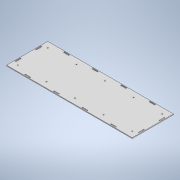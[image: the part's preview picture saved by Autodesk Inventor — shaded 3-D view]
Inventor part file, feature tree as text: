
AUTODESK INVENTOR PART (.ipt)
format: ipt  version: 2022 (Build 260153000, 153)  size: 268,288 bytes
history: native  units: in
note: dims shown in document units (in); Inventor stores cm internally (conversion verified against a paired STEP export)
features: extrude x1, sketch x1
ambient origin geometry x8: Origin, YZ Plane, XZ Plane, XY Plane, X Axis, Y Axis, Z Axis, Center Point
bodies: Body1 (feature_tree)
feature tree (2):
  extrude  "Extrusion2"  Depth=0.1181in
  sketch  "Sketch1"  dims[d0=20.0in d1=12.0in d2=19.685in d3=11.811in d6=2.7559in d8=1.1811in d10=3.4252in d11=1.1811in d13=3.4252in d38=0.5512in d60=0.1181in d61=0.0in d63=18.5039in d67=6.063in d68=16.4567in d71=0.1457in d72=0.1969in d73=0.1969in d74=4.2126in d75=4.2126in d76=4.2126in d77=4.2126in d78=0.1181in d79=0.7874in d80=0.1181in d81=6.3189in d82=0.7874in d83=0.1181in d84=0.1181in d85=1.5748in d87=4.2126in d88=0.3937in d90=0.3937in d92=0.1181in d93=0.7874in d94=1.5157in d95=0.1181in d96=0.1181in d97=0.7874in d98=0.1181in d99=1.5157in d100=0.1181in d101=0.7874in d102=0.1181in d103=0.7874in d104=0.1181in]
